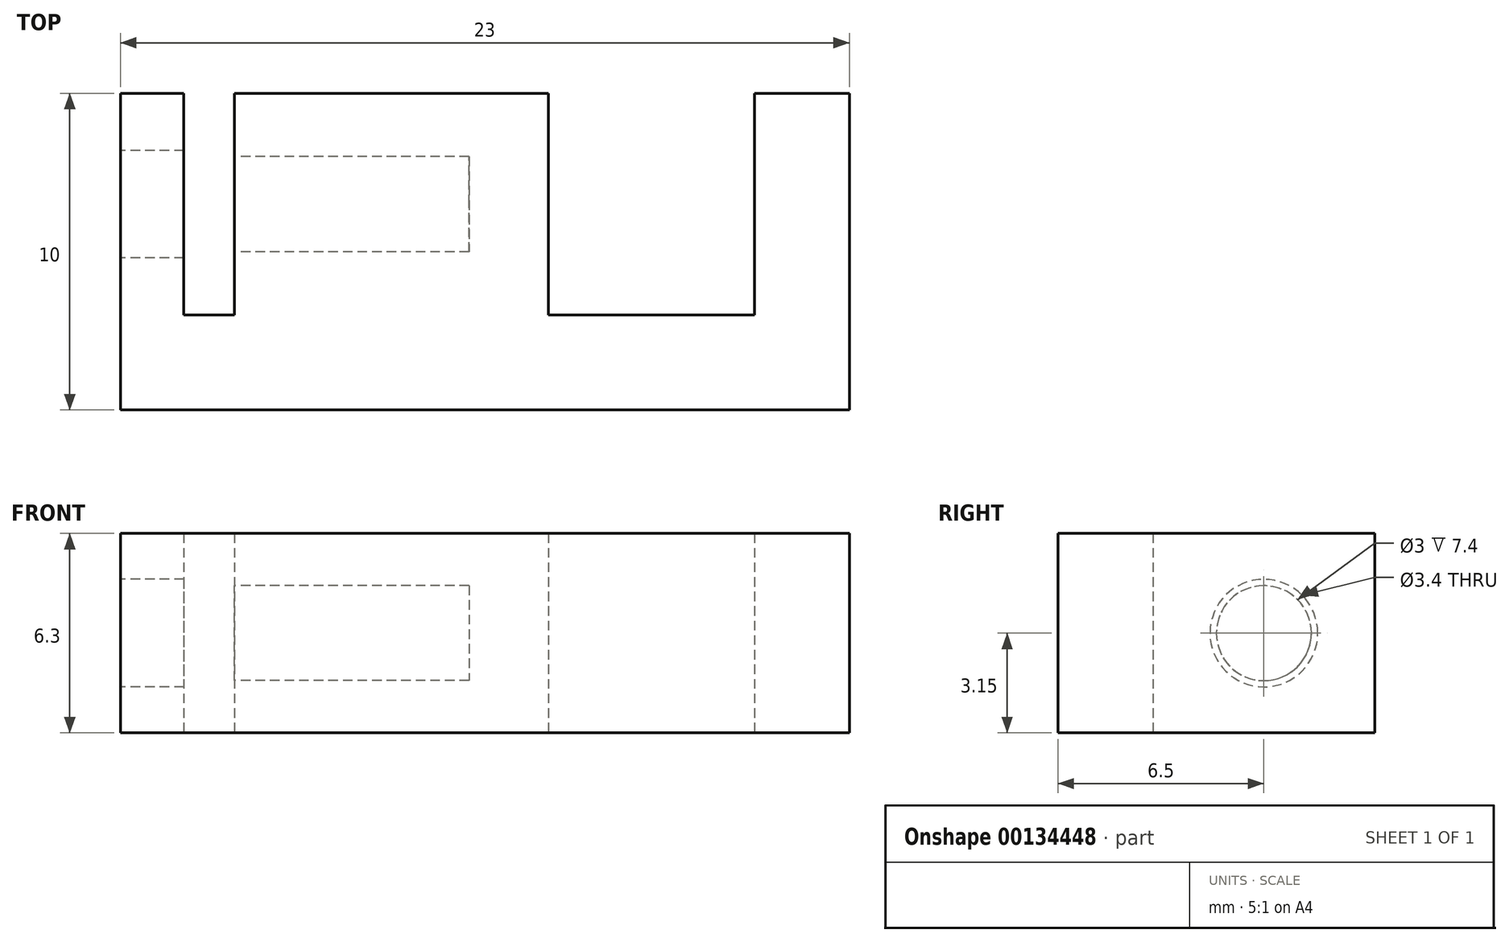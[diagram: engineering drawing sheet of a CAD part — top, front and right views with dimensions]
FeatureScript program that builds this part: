
annotation { "Feature Type Name" : "Feature", "Feature Type Description" : "" }
export const myFeature = defineFeature(function(context is Context, id is Id, definition is map)
    precondition{}
    {
        {
            var Q0;
            Q0=qCreatedBy(makeId("Top.planeOp"),FACE);
            var sketch = newSketch(context, id + "F0", { "sketchPlane" : qUnion([Q0])});
            skLineSegment(sketch, "E0", {"start": v(-11.5, 5) * mm, "end": v(-11.5, -5) * mm});
            skLineSegment(sketch, "E1", {"start": v(-11.5, -5) * mm, "end": v(11.5, -5) * mm});
            skLineSegment(sketch, "E2", {"start": v(11.5, -5) * mm, "end": v(11.5, 5) * mm});
            skLineSegment(sketch, "E3", {"start": v(11.5, 5) * mm, "end": v(8.5, 5) * mm});
            skLineSegment(sketch, "E4", {"start": v(8.5, 5) * mm, "end": v(8.5, -2) * mm});
            skLineSegment(sketch, "E5", {"start": v(8.5, -2) * mm, "end": v(2, -2) * mm});
            skLineSegment(sketch, "E6", {"start": v(2, -2) * mm, "end": v(2, 5) * mm});
            skLineSegment(sketch, "E7", {"start": v(2, 5) * mm, "end": v(-7.9, 5) * mm});
            skLineSegment(sketch, "E8", {"start": v(-7.9, 5) * mm, "end": v(-7.9, -2) * mm});
            skLineSegment(sketch, "E9", {"start": v(-7.9, -2) * mm, "end": v(-9.5, -2) * mm});
            skLineSegment(sketch, "E10", {"start": v(-9.5, -2) * mm, "end": v(-9.5, 5) * mm});
            skLineSegment(sketch, "E11", {"start": v(-9.5, 5) * mm, "end": v(-11.5, 5) * mm});
            skPoint(sketch, "E12", {"position": v(-11.5, 0) * mm});
            skPoint(sketch, "E13", {"position": v(0, -5) * mm});
            skSolve(sketch);
        }
        {
            var Q0;
            Q0=qSketchRegion(id+"F0",true);
            extrude(context, id + "F1", {"entities" : qUnion([Q0]), "endBound" : BoundingType.SYMMETRIC, "depth" : 6.3 * mm});
        }
        {
            var Q0;
            Q0=makeQuery(id+"F1.opExtrude","SWEPT_FACE",FACE,{"disambiguationData":[OSD([sQuery(id+"F0.wireOp",EDGE,"E0")])]});
            var sketch = newSketch(context, id + "F2", { "sketchPlane" : qUnion([Q0])});
            skCircle(sketch, "E14", {"center": v(-1.5, 0) * mm, "radius": 1.5 * mm});
            skCircle(sketch, "E15.0", {"center": v(-1.5, 0) * mm, "radius": 1.7 * mm});
            skSolve(sketch);
        }
        {
            var Q0;
            Q0=makeQuery(id+"F2.imprint","IMPRINT",FACE,{"disambiguationData":[TD([[makeQuery(id+"F2.imprint","IMPRINT",EDGE,{"derivedFrom":sQuery(id+"F2.wireOp",EDGE,"E14")}),1.0]])]});
            extrude(context, id + "F3", {"entities" : qUnion([Q0]), "operationType" : NewBodyOperationType.REMOVE, "oppositeDirection" : true, "depth" : 11 * mm});
        }
        {
            var Q0;
            Q0=makeQuery(id+"F2.imprint","IMPRINT",FACE,{"disambiguationData":[TD([[makeQuery(id+"F2.imprint","IMPRINT",EDGE,{"derivedFrom":sQuery(id+"F2.wireOp",EDGE,"E14")}),-1.0]])]});
            extrude(context, id + "F4", {"entities" : qUnion([Q0]), "operationType" : NewBodyOperationType.REMOVE, "endBound" : BoundingType.UP_TO_NEXT, "oppositeDirection" : true, "depth" : 25 * mm});
        }
    });
